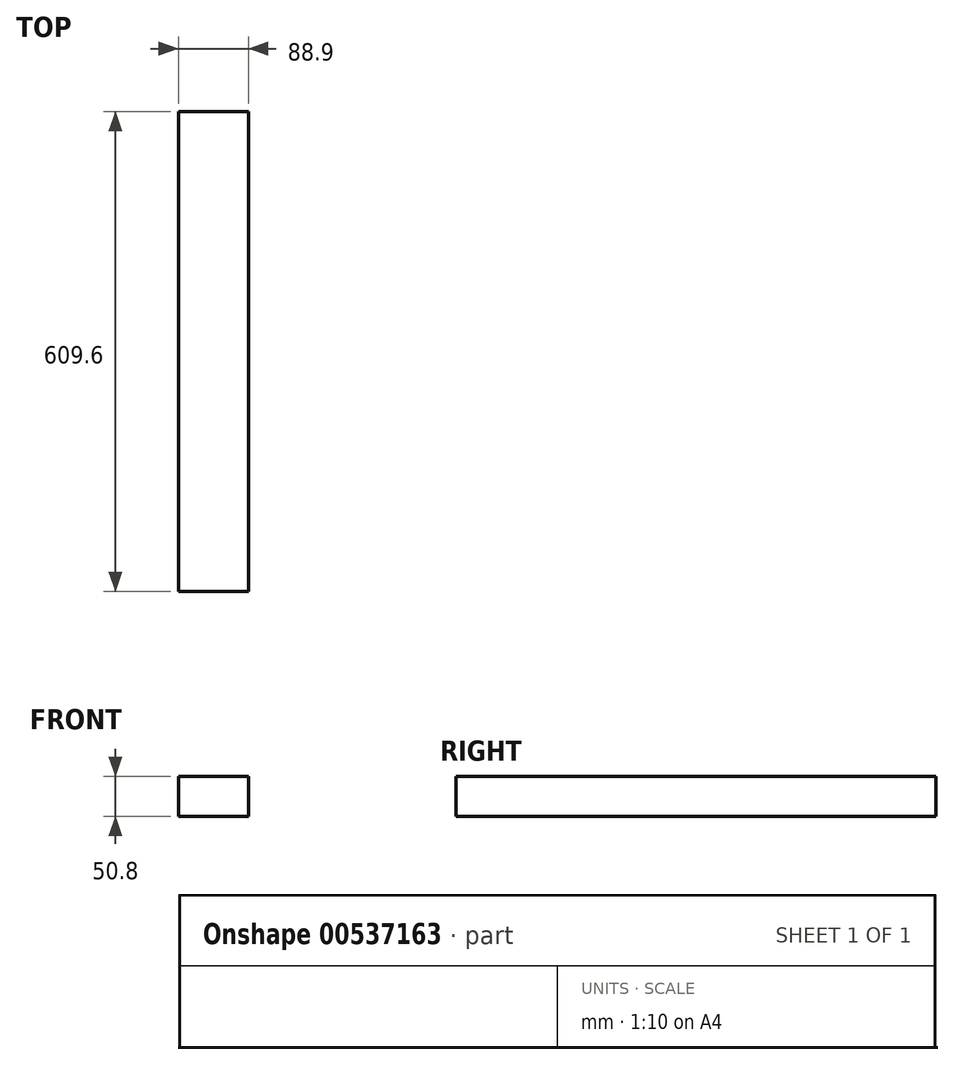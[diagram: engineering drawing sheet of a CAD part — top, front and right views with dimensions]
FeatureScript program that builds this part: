
annotation { "Feature Type Name" : "Feature", "Feature Type Description" : "" }
export const myFeature = defineFeature(function(context is Context, id is Id, definition is map)
    precondition{}
    {
        {
            var Q0;
            Q0=qCreatedBy(makeId("Front.planeOp"),FACE);
            var sketch = newSketch(context, id + "F0", { "sketchPlane" : qUnion([Q0])});
            skLineSegment(sketch, "E0.bottom", {"start": v(-63.8, 31.29) * mm, "end": v(25.1, 31.29) * mm});
            skLineSegment(sketch, "E0.top", {"start": v(-63.8, -19.51) * mm, "end": v(25.1, -19.51) * mm});
            skLineSegment(sketch, "E0.left", {"start": v(-63.8, 31.29) * mm, "end": v(-63.8, -19.51) * mm});
            skLineSegment(sketch, "E0.right", {"start": v(25.1, 31.29) * mm, "end": v(25.1, -19.51) * mm});
            skSolve(sketch);
        }
        {
            var Q0;
            Q0 = qSketchRegion(id + "F0", true);
            extrude(context, id + "F1", {"entities" : qUnion([Q0]), "depth" : 609.6 * mm, "offsetDistance" : 25.4 * mm});
        }
    });
